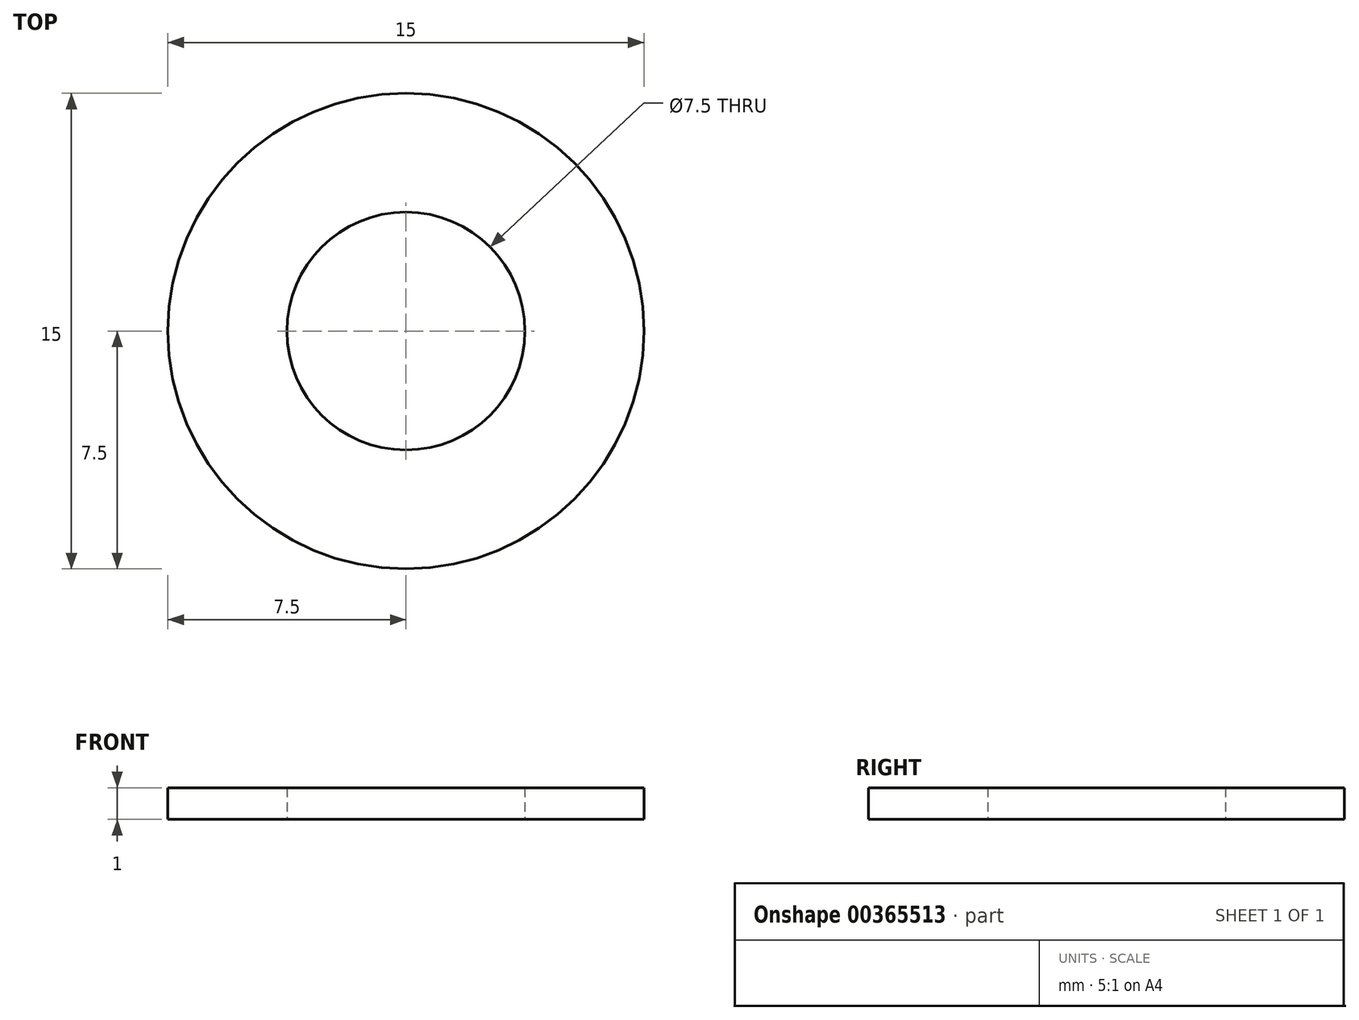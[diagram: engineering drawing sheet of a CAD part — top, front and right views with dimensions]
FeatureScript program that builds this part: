
annotation { "Feature Type Name" : "Feature", "Feature Type Description" : "" }
export const myFeature = defineFeature(function(context is Context, id is Id, definition is map)
    precondition{}
    {
        {
            var Q0;
            Q0=qCreatedBy(makeId("Top.planeOp"),FACE);
            var sketch = newSketch(context, id + "F0", { "sketchPlane" : qUnion([Q0])});
            skCircle(sketch, "E0", {"center": v(0, 0) * mm, "radius": 7.5 * mm});
            skCircle(sketch, "E1", {"center": v(0, 0) * mm, "radius": 3.75 * mm});
            skSolve(sketch);
        }
        {
            var Q0;
            Q0 = qSketchRegion(id + "F0", true);
            extrude(context, id + "F1", {"entities" : qUnion([Q0]), "depth" : 1 * mm});
        }
    });
